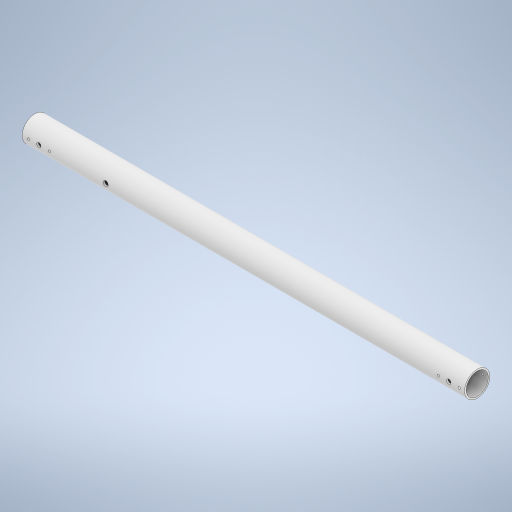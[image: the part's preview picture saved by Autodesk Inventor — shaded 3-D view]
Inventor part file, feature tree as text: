
AUTODESK INVENTOR PART (.ipt)
format: ipt  version: 2023 (Build 270158030, 158C)  size: 300,544 bytes
history: native  units: in
note: dims shown in document units (in); Inventor stores cm internally (conversion verified against a paired STEP export)
features: extrude x4, sketch x4
ambient origin geometry x8: Origin, YZ Plane, XZ Plane, XY Plane, X Axis, Y Axis, Z Axis, Center Point
bodies: Solid1 (feature_tree)
feature tree (8):
  extrude  "Extrusion1"  Depth=0.154in
  extrude  "Extrusion3"  Depth=0.4134in
  extrude  "Extrusion5"  TaperAngle=0.0deg  [1 undecoded]
  extrude  "Extrusion6"  Depth=0.1969in
  sketch  "Sketch1"  dims[d0=2.067in d1=0.154in]
  sketch  "Sketch3"  dims[d2=41.7323in d3=0.0in d8=0.4134in]
  sketch  "Sketch5"  dims[d9=1.5in d10=0.0in d11=0.0in]
  sketch  "Sketch6"  dims[d17=0.4724in d18=7.874in d19=0.0in d20=0.0in d21=0.3937in d22=1.5748in d23=0.0in d24=0.0in d25=1.9685in d26=0.1969in d27=1.9685in d28=0.2165in]
note: 1 required parameter value undecoded (feature->parameter linkage not recoverable at this tier; creation-order binding heuristic only, values carry confidence <= 0.55)
